FCSTD DOCUMENT  (FreeCAD 1.0R39319 (Git))
Label: 00_MasterLayout
License: All rights reserved
LicenseURL: https://en.wikipedia.org/wiki/All_rights_reserved
objects: PartDesign::Plane×4, Sketcher::SketchObject×2, PartDesign::Body×1, App::Link×1
note: 9 computed .brp shape members not serialized (recipe doc carries the construction recipe); baked Part::Feature solids carry a one-line shape summary decoded from their .brp
EXTERNAL_REF file=Airfoil-Wing.FCStd obj=AeroFoil_1

FEATURE [PartDesign::Plane] DatumPlane  label="PLN_Centerline"
  AttachmentSupport = -> [XZ_Plane]
  Length = 3614.02
  MapMode = 5
  Placement = pos=(0,0,0) rot=(1,0,0;1.5708rad)
  ResizeMode = 0
  Width = 134.024
FEATURE [PartDesign::Plane] DatumPlane001  label="PLN_Ground"
  AttachmentSupport = -> [XY_Plane]
  Length = 4144.29
  MapMode = 5
  ResizeMode = 0
  Width = 3286.74
FEATURE [PartDesign::Plane] DatumPlane002  label="PLN_WingRef"
  AttachmentOffset = pos=(0,0,500) rot=(0,0,1;0rad)
  AttachmentSupport = -> [XY_Plane]
  Length = 4144.29
  MapMode = 5
  Placement = pos=(0,0,500) rot=(0,0,1;0rad)
  ResizeMode = 0
  Width = 3286.74
FEATURE [PartDesign::Plane] DatumPlane003  label="PLN_RotorHub"
  AttachmentOffset = pos=(0,0,600) rot=(0,0,1;0rad)
  AttachmentSupport = -> [XY_Plane]
  Length = 4144.29
  MapMode = 5
  Placement = pos=(0,0,600) rot=(0,0,1;0rad)
  ResizeMode = 0
  Width = 3286.74
FEATURE [Sketcher::SketchObject] Sketch001  label="SK_TopView_Layout"
  ArcFitTolerance = 1e-06
  AttachmentSupport = -> [XY_Plane]
  FullyConstrained = true
  MakeInternals = false
  MapMode = 5
  sketch-geometry (24):
    g0: LineSegment [constr] StartX=0 StartY=2000 StartZ=0 EndX=0 EndY=-2000 EndZ=0
    g1: LineSegment StartX=-1415 StartY=-175 StartZ=0 EndX=1415 EndY=-175 EndZ=0
    g2: LineSegment StartX=1415 StartY=-175 StartZ=0 EndX=1415 EndY=175 EndZ=0
    g3: LineSegment StartX=1415 StartY=175 StartZ=0 EndX=-1415 EndY=175 EndZ=0
    g4: LineSegment StartX=-1415 StartY=175 StartZ=0 EndX=-1415 EndY=-175 EndZ=0
    g5: GeomPoint [constr] X=-9e-16 Y=0 Z=0
    g6: LineSegment StartX=-300 StartY=1000 StartZ=0 EndX=-300 EndY=-1500 EndZ=0
    g7: LineSegment StartX=-300 StartY=-1500 StartZ=0 EndX=300 EndY=-1500 EndZ=0
    g8: LineSegment StartX=300 StartY=-1500 StartZ=0 EndX=300 EndY=1000 EndZ=0
    g9: LineSegment StartX=300 StartY=1000 StartZ=0 EndX=-300 EndY=1000 EndZ=0
    g10: GeomPoint X=-1415 Y=-8e-16 Z=0
    g11: Circle CenterX=1415 CenterY=-8e-16 CenterZ=0 NormalX=0 NormalY=0 NormalZ=1 AngleXU=0 Radius=350
    g12: GeomPoint X=1415 Y=-8e-16 Z=0
    g13: LineSegment StartX=-550 StartY=-1500 StartZ=0 EndX=550 EndY=-1500 EndZ=0
    g14: LineSegment StartX=550 StartY=-1500 StartZ=0 EndX=550 EndY=-1150 EndZ=0
    g15: LineSegment StartX=550 StartY=-1150 StartZ=0 EndX=-550 EndY=-1150 EndZ=0
    g16: LineSegment StartX=-550 StartY=-1150 StartZ=0 EndX=-550 EndY=-1500 EndZ=0
    g17: GeomPoint [constr] X=0 Y=-1325 Z=0
    g18: Circle CenterX=-1415 CenterY=-8e-16 CenterZ=0 NormalX=0 NormalY=0 NormalZ=1 AngleXU=0 Radius=350
    g19: Circle CenterX=550 CenterY=-1325 CenterZ=0 NormalX=0 NormalY=0 NormalZ=1 AngleXU=0 Radius=350
    g20: Circle CenterX=-550 CenterY=-1325 CenterZ=0 NormalX=0 NormalY=0 NormalZ=1 AngleXU=0 Radius=350
    g21: GeomPoint X=-550 Y=-1325 Z=0
    g22: GeomPoint X=550 Y=-1325 Z=0
    g23: GeomPoint X=0 Y=87.5 Z=0
  constraints (55):
    c: Parallel(g0,g-2)
    c: PointOnObject(g-1,g0)
    c: DistanceY(g0,g0) = 4000
    c: DistanceY(g-1,g0) = 2000
    c: Coincident(g1,g2)
    c: Coincident(g2,g3)
    c: Coincident(g3,g4)
    c: Coincident(g4,g1)
    c: Horizontal(g1)
    c: Horizontal(g3)
    c: Vertical(g2)
    c: Vertical(g4)
    c: Symmetric(g3,g1,g5)
    c: Distance(g2,g4) = 2830
    c: Distance(g1,g3) = 350
    c: Coincident(g5,g-1)
    c: Coincident(g6,g7)
    c: Coincident(g7,g8)
    c: Coincident(g8,g9)
    c: Coincident(g9,g6)
    c: Vertical(g6)
    c: Vertical(g8)
    c: Horizontal(g7)
    c: Horizontal(g9)
    c: Distance(g6,g8) = 600
    c: Distance(g7,g9) = 2500
    c: Distance(g6,g0) = 300
    c: Distance(g9,g-1) = 1000
    c: Symmetric(g4,g4,g10)
    c: Diameter(g11) = 700
    c: Symmetric(g2,g2,g12)
    c: Coincident(g11,g12)
    c: Coincident(g13,g14)
    c: Coincident(g14,g15)
    c: Coincident(g15,g16)
    c: Coincident(g16,g13)
    c: Horizontal(g13)
    c: Horizontal(g15)
    c: Vertical(g14)
    c: Vertical(g16)
    c: Symmetric(g15,g13,g17)
    c: Distance(g14,g16) = 1100
    c: Distance(g13,g15) = 350
    c: PointOnObject(g17,g0)
    c: Distance(g17,g7) = 175
    c: Diameter(g18) = 700
    c: Diameter(g20) = 700
    c: Diameter(g19) = 700
    c: Symmetric(g16,g16,g21)
    c: Symmetric(g14,g14,g22)
    c: Coincident(g20,g21)
    c: Coincident(g19,g22)
    c: Coincident(g18,g10)
    c: PointOnObject(g23,g0)
    c: Distance(g23,g3) = 87.5
FEATURE [Sketcher::SketchObject] Sketch  label="SK_SideView_Layout"
  ArcFitTolerance = 1e-06
  AttachmentSupport = -> [YZ_Plane]
  FullyConstrained = true
  MakeInternals = false
  MapMode = 5
  Placement = pos=(0,0,0) rot=(0.57735,0.57735,0.57735;2.0944rad)
  sketch-geometry (27):
    g0: LineSegment [constr] StartX=-2000 StartY=0 StartZ=0 EndX=2000 EndY=0 EndZ=0
    g1: LineSegment StartX=-1500 StartY=300 StartZ=0 EndX=-1500 EndY=-300 EndZ=0
    g2: LineSegment StartX=-1500 StartY=-300 StartZ=0 EndX=1000 EndY=-300 EndZ=0
    g3: LineSegment StartX=1000 StartY=-300 StartZ=0 EndX=1000 EndY=300 EndZ=0
    g4: LineSegment StartX=1000 StartY=300 StartZ=0 EndX=-1500 EndY=300 EndZ=0
    g5: LineSegment StartX=-1500 StartY=242 StartZ=0 EndX=-1500 EndY=200 EndZ=0
    g6: LineSegment StartX=-1500 StartY=200 StartZ=0 EndX=-1150 EndY=200 EndZ=0
    g7: LineSegment StartX=-1150 StartY=200 StartZ=0 EndX=-1150 EndY=242 EndZ=0
    g8: LineSegment StartX=-1150 StartY=242 StartZ=0 EndX=-1500 EndY=242 EndZ=0
    g9: LineSegment StartX=-1500 StartY=242 StartZ=0 EndX=-1150 EndY=242 EndZ=0
    g10: LineSegment StartX=-1150 StartY=242 StartZ=0 EndX=-1150 EndY=692 EndZ=0
    g11: LineSegment StartX=-1150 StartY=692 StartZ=0 EndX=-1500 EndY=692 EndZ=0
    g12: LineSegment StartX=-1500 StartY=692 StartZ=0 EndX=-1500 EndY=242 EndZ=0
    g13: Ellipse CenterX=0 CenterY=279 CenterZ=0 NormalX=0 NormalY=0 NormalZ=1 MajorRadius=350 MinorRadius=60 AngleXU=-1.5708
    g14: LineSegment [constr] StartX=0 StartY=-71 StartZ=0 EndX=0 EndY=629 EndZ=0
    g15: GeomPoint [constr] X=3.83e-14 Y=-65.8188 Z=0
    g16: GeomPoint [constr] X=0 Y=623.819 Z=0
    g17: Ellipse CenterX=-1325 CenterY=692 CenterZ=0 NormalX=0 NormalY=0 NormalZ=1 MajorRadius=350 MinorRadius=60 AngleXU=-1.5708
    g18: LineSegment [constr] StartX=-1325 StartY=342 StartZ=0 EndX=-1325 EndY=1042 EndZ=0
    g19: LineSegment [constr] StartX=-1265 StartY=692 StartZ=0 EndX=-1385 EndY=692 EndZ=0
    g20: GeomPoint [constr] X=-1325 Y=347.181 Z=0
    g21: GeomPoint [constr] X=-1325 Y=1036.82 Z=0
    g22: LineSegment StartX=-175 StartY=258 StartZ=0 EndX=175 EndY=258 EndZ=0
    g23: LineSegment StartX=175 StartY=258 StartZ=0 EndX=175 EndY=300 EndZ=0
    g24: LineSegment StartX=175 StartY=300 StartZ=0 EndX=-175 EndY=300 EndZ=0
    g25: LineSegment StartX=-175 StartY=300 StartZ=0 EndX=-175 EndY=258 EndZ=0
    g26: GeomPoint [constr] X=0 Y=279 Z=0
  constraints (65):
    c: DistanceX(g0,g0) = 4000
    c: PointOnObject(g-1,g0)
    c: Parallel(g0,g-1)
    c: DistanceX(g-1,g0) = 2000
    c: Coincident(g1,g2)
    c: Coincident(g2,g3)
    c: Coincident(g3,g4)
    c: Coincident(g4,g1)
    c: Vertical(g1)
    c: Vertical(g3)
    c: Horizontal(g2)
    c: Horizontal(g4)
    c: Distance(g1,g3) = 2500
    c: Distance(g2,g4) = 600
    c: Distance(g0,g4) = 300
    c: Distance(g-1,g3) = 1000
    c: Coincident(g5,g6)
    c: Coincident(g6,g7)
    c: Coincident(g7,g8)
    c: Coincident(g8,g5)
    c: Vertical(g5)
    c: Vertical(g7)
    c: Horizontal(g6)
    c: Horizontal(g8)
    c: Distance(g5,g7) = 350
    c: Distance(g6,g8) = 42
    c: PointOnObject(g5,g1)
    c: Distance(g6,g0) = 200
    c: Coincident(g9,g10)
    c: Coincident(g10,g11)
    c: Coincident(g11,g12)
    c: Coincident(g12,g9)
    c: Horizontal(g9)
    c: Horizontal(g11)
    c: Vertical(g10)
    c: Vertical(g12)
    c: Distance(g10,g12) = 350
    c: Distance(g9,g11) = 450
    c: Coincident(g9,g5)
    c: InternalAlignment(g14,g13)
    c: InternalAlignment(g15,g13)
    c: InternalAlignment(g16,g13)
    c: Distance(g13,g14) = 350
    c: PointOnObject(g14,g-2)
    c: InternalAlignment(g18-g21 -> g17) x4
    c: Distance(g17,g18) = 350
    c: Distance(g17,g19) = 60
    c: PointOnObject(g17,g11)
    c: DistanceX(g11,g17) = 175
    c: Parallel(g18,g12)
    c: Coincident(g22,g23)
    c: Coincident(g23,g24)
    c: Coincident(g24,g25)
    c: Coincident(g25,g22)
    c: Horizontal(g22)
    c: Horizontal(g24)
    c: Vertical(g23)
    c: Vertical(g25)
    c: Symmetric(g24,g22,g26)
    c: Distance(g23,g25) = 350
    c: Distance(g22,g24) = 42
    c: PointOnObject(g26,g-2)
    c: PointOnObject(g23,g4)
    c: Coincident(g26,g13)
    c: DistanceY(g16,g14) = 5.18121
FEATURE [PartDesign::Body] Body
  AllowCompound = false
  Group = -> [DatumPlane,DatumPlane001,DatumPlane002,DatumPlane003,Sketch001,Sketch]
  Origin = -> Origin
FEATURE [App::Link] Link  label="AeroFoil_1"
  LinkPlacement = pos=(0,0,0) rot=(0.58,0.58,0.58;2.0944rad)
  LinkedObject = -> <external Airfoil-Wing.FCStd>#AeroFoil_1
  Placement = pos=(0,0,0) rot=(0.58,0.58,0.58;2.0944rad)
